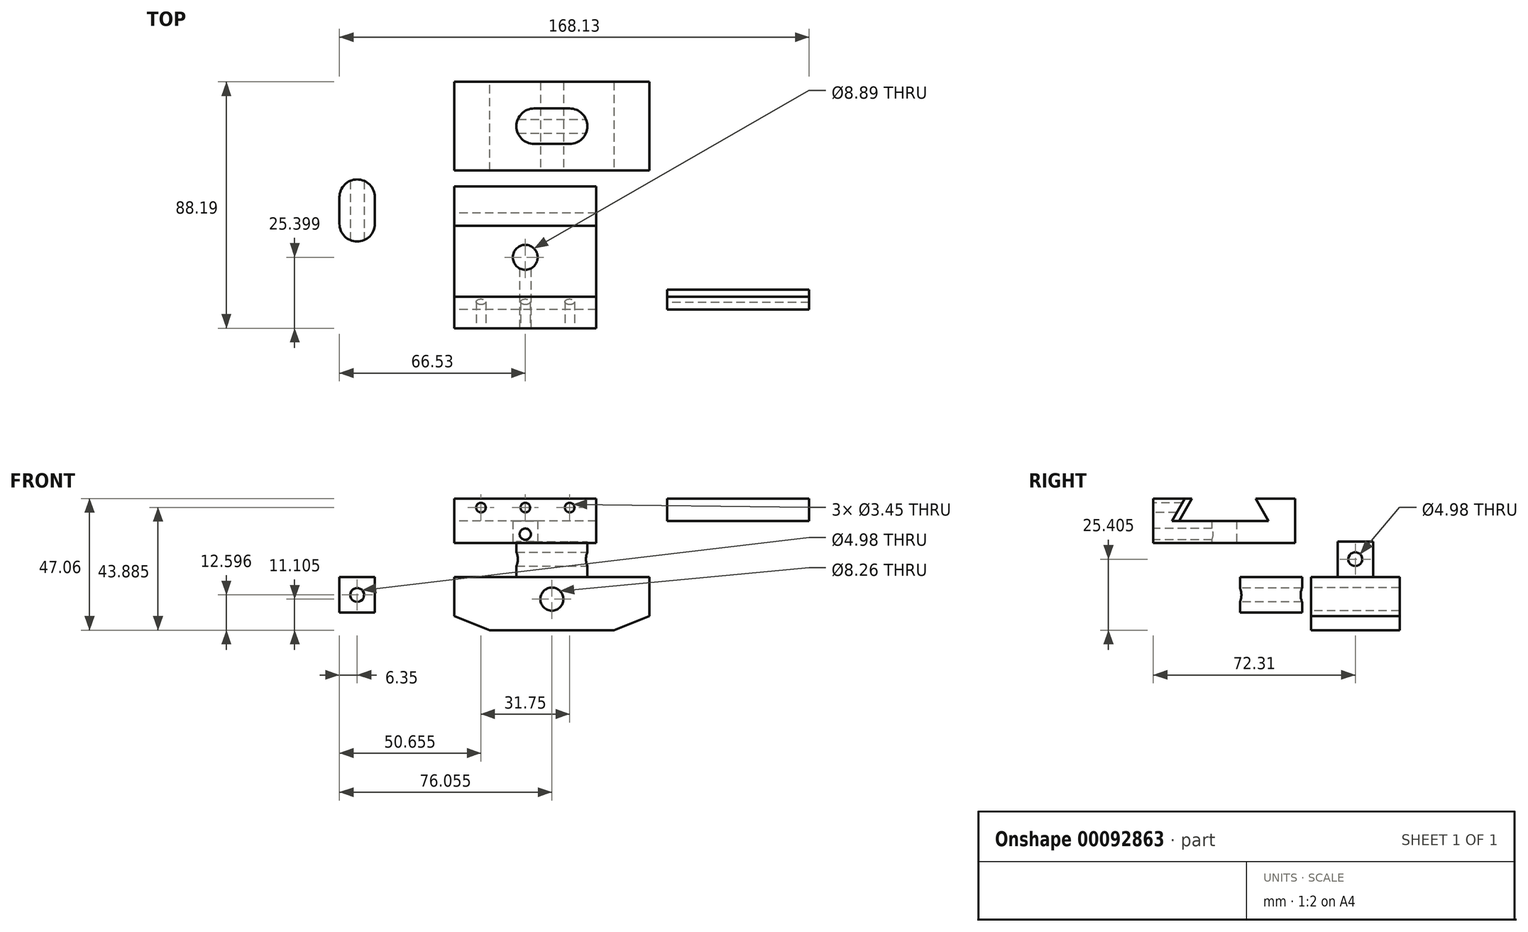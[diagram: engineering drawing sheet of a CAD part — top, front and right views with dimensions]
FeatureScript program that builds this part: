
annotation { "Feature Type Name" : "Feature", "Feature Type Description" : "" }
export const myFeature = defineFeature(function(context is Context, id is Id, definition is map)
    precondition{}
    {
        {
            var Q0;
            Q0=qCreatedBy(makeId("Right.planeOp"),FACE);
            var sketch = newSketch(context, id + "F0", { "sketchPlane" : qUnion([Q0])});
            skLineSegment(sketch, "E0.bottom", {"start": v(15.88, -15.87) * mm, "end": v(-15.88, -15.88) * mm});
            skLineSegment(sketch, "E0.top", {"start": v(15.88, 15.88) * mm, "end": v(-15.88, 15.88) * mm});
            skLineSegment(sketch, "E0.left", {"start": v(15.88, -15.87) * mm, "end": v(15.88, 7.62) * mm});
            skLineSegment(sketch, "E0.right", {"start": v(-15.88, -15.88) * mm, "end": v(-15.88, 7.62) * mm});
            skPoint(sketch, "E0.middle", {"position": v(0, 0) * mm});
            skLineSegment(sketch, "E1", {"start": v(-15.88, 7.62) * mm, "end": v(15.88, 7.62) * mm, "construction": true});
            skLineSegment(sketch, "E2", {"start": v(15.88, 15.88) * mm, "end": v(11.1, 7.62) * mm});
            skLineSegment(sketch, "E3", {"start": v(-15.88, 15.88) * mm, "end": v(-11.1, 7.62) * mm});
            skLineSegment(sketch, "E4", {"start": v(-15.88, 7.62) * mm, "end": v(-11.1, 7.62) * mm});
            skLineSegment(sketch, "E5", {"start": v(11.1, 7.62) * mm, "end": v(15.88, 7.62) * mm});
            skSolve(sketch);
        }
        {
            var Q0;
            Q0=makeQuery(id+"F0.imprint","IMPRINT",FACE,{"disambiguationData":[TD([[makeQuery(id+"F0.imprint","IMPRINT",EDGE,{"derivedFrom":sQuery(id+"F0.wireOp",EDGE,"E0.bottom")}),-1.0]])]});
            extrude(context, id + "F1", {"entities" : qUnion([Q0]), "depth" : 69.85 * mm});
        }
        {
            var Q0;
            Q0=makeQuery(id+"F1.opExtrude","CAP_FACE",FACE,{"disambiguationData":[OSD([sQuery(id+"F0.wireOp",EDGE,"E0.bottom"),sQuery(id+"F0.wireOp",EDGE,"E0.top"),sQuery(id+"F0.wireOp",EDGE,"E0.left"),sQuery(id+"F0.wireOp",EDGE,"E0.right"),sQuery(id+"F0.wireOp",EDGE,"E2"),sQuery(id+"F0.wireOp",EDGE,"E3"),sQuery(id+"F0.wireOp",EDGE,"E4"),sQuery(id+"F0.wireOp",EDGE,"E5")])],"isStart":false});
            var sketch = newSketch(context, id + "F2", { "sketchPlane" : qUnion([Q0])});
            skLineSegment(sketch, "E6", {"start": v(-12.2, 9.52) * mm, "end": v(12.2, 9.52) * mm, "construction": true});
            skPoint(sketch, "E7", {"position": v(0, 9.52) * mm});
            skSolve(sketch);
        }
        {
            var Q0;
            Q0=sQuery(id+"F2.wireOp",VERTEX,"E7");
            var Q1;
            Q1=makeQuery(id+"F1.opExtrude","SWEPT_BODY",BODY,{"disambiguationData":[OSD([sQuery(id+"F0.wireOp",EDGE,"E0.bottom"),sQuery(id+"F0.wireOp",EDGE,"E0.top"),sQuery(id+"F0.wireOp",EDGE,"E0.left"),sQuery(id+"F0.wireOp",EDGE,"E0.right"),sQuery(id+"F0.wireOp",EDGE,"E2"),sQuery(id+"F0.wireOp",EDGE,"E3"),sQuery(id+"F0.wireOp",EDGE,"E4"),sQuery(id+"F0.wireOp",EDGE,"E5")])]});
            hole(context, id + "F3", {"style" : HoleStyle.SIMPLE, "endStyle" : HoleEndStyle.THROUGH, "standardTappedOrClearance" : lookupTablePath({ "standard" : "ANSI", "fit" : "Close", "size" : "#10", "type" : "Clearance" }), "standardBlindInLast" : lookupTablePath({ "fit" : "Close", "standard" : "ANSI", "size" : "#10", "type" : "Clearance" }), "holeDiameter" : 4.98 * mm, "locations" : qUnion([Q0]), "scope" : qUnion([Q1]), "isTappedThrough" : true});
        }
        {
            var Q0;
            Q0=makeQuery(id+"F1.opExtrude","SWEPT_FACE",FACE,{"disambiguationData":[OSD([sQuery(id+"F0.wireOp",EDGE,"E0.right")])]});
            var sketch = newSketch(context, id + "F4", { "sketchPlane" : qUnion([Q0])});
            skLineSegment(sketch, "E8.0.0", {"start": v(0, 7.62) * mm, "end": v(0, -15.88) * mm, "construction": true});
            skLineSegment(sketch, "E8.0.1", {"start": v(0, -15.88) * mm, "end": v(69.85, -15.88) * mm, "construction": true});
            skLineSegment(sketch, "E8.0.2", {"start": v(69.85, -15.88) * mm, "end": v(69.85, 7.62) * mm, "construction": true});
            skLineSegment(sketch, "E8.0.3", {"start": v(69.85, 7.62) * mm, "end": v(0, 7.62) * mm, "construction": true});
            skLineSegment(sketch, "E9", {"start": v(0, -4.78) * mm, "end": v(69.85, -4.78) * mm, "construction": true});
            skPoint(sketch, "E10", {"position": v(34.93, -4.78) * mm});
            skSolve(sketch);
        }
        {
            var Q0;
            Q0=sQuery(id+"F4.wireOp",VERTEX,"E10");
            var Q1;
            Q1=makeQuery(id+"F1.opExtrude","SWEPT_BODY",BODY,{"disambiguationData":[OSD([sQuery(id+"F0.wireOp",EDGE,"E0.bottom"),sQuery(id+"F0.wireOp",EDGE,"E0.top"),sQuery(id+"F0.wireOp",EDGE,"E0.left"),sQuery(id+"F0.wireOp",EDGE,"E0.right"),sQuery(id+"F0.wireOp",EDGE,"E2"),sQuery(id+"F0.wireOp",EDGE,"E3"),sQuery(id+"F0.wireOp",EDGE,"E4"),sQuery(id+"F0.wireOp",EDGE,"E5")])]});
            hole(context, id + "F5", {"style" : HoleStyle.SIMPLE, "endStyle" : HoleEndStyle.THROUGH, "holeDiameter" : 8.25 * mm, "locations" : qUnion([Q0]), "scope" : qUnion([Q1]), "isTappedThrough" : true});
        }
        {
            var Q0;
            Q0=makeQuery(id+"F1.opExtrude","SWEPT_FACE",FACE,{"disambiguationData":[OSD([sQuery(id+"F0.wireOp",EDGE,"E0.top")])]});
            var sketch = newSketch(context, id + "F6", { "sketchPlane" : qUnion([Q0])});
            skLineSegment(sketch, "E11.0.0", {"start": v(0, 15.88) * mm, "end": v(0, -15.88) * mm, "construction": true});
            skLineSegment(sketch, "E11.0.1", {"start": v(0, -15.88) * mm, "end": v(69.85, -15.88) * mm, "construction": true});
            skLineSegment(sketch, "E11.0.2", {"start": v(69.85, -15.88) * mm, "end": v(69.85, 15.88) * mm, "construction": true});
            skLineSegment(sketch, "E11.0.3", {"start": v(69.85, 15.88) * mm, "end": v(0, 15.88) * mm, "construction": true});
            skLineSegment(sketch, "E12", {"start": v(28.58, 15.88) * mm, "end": v(28.58, -15.88) * mm, "construction": true});
            skLineSegment(sketch, "E13", {"start": v(41.28, 15.88) * mm, "end": v(41.28, -15.88) * mm, "construction": true});
            skLineSegment(sketch, "E14", {"start": v(0, 0) * mm, "end": v(69.85, 0) * mm, "construction": true});
            skLineSegment(sketch, "E15", {"start": v(28.58, 0) * mm, "end": v(41.28, 0) * mm});
            skArc(sketch, "E16.0.startCap", {"start": v(28.58, -6.35) * mm, "mid": v(22.23, 0) * mm, "end": v(28.58, 6.35) * mm});
            skArc(sketch, "E16.0.endCap", {"start": v(41.28, 6.35) * mm, "mid": v(47.63, 0) * mm, "end": v(41.28, -6.35) * mm});
            skLineSegment(sketch, "E16.0.left", {"start": v(28.58, 6.35) * mm, "end": v(41.28, 6.35) * mm});
            skLineSegment(sketch, "E16.0.right", {"start": v(28.58, -6.35) * mm, "end": v(41.28, -6.35) * mm});
            skSolve(sketch);
        }
        {
            var Q0;
            Q0=makeQuery(id+"F6.imprint","IMPRINT",FACE,{"disambiguationData":[TD([[makeQuery(id+"F6.imprint","IMPRINT",EDGE,{"derivedFrom":sQuery(id+"F6.wireOp",EDGE,"E16.0.startCap")}),-1.0]])]});
            extrude(context, id + "F7", {"entities" : qUnion([Q0]), "operationType" : NewBodyOperationType.REMOVE, "oppositeDirection" : true, "depth" : 12.7 * mm});
        }
        {
            var Q0;
            Q0=qCreatedBy(makeId("Front.planeOp"),FACE);
            var sketch = newSketch(context, id + "F8", { "sketchPlane" : qUnion([Q0])});
            skLineSegment(sketch, "E17.bottom", {"start": v(-50.66, 3.07) * mm, "end": v(-18.9, 3.07) * mm});
            skLineSegment(sketch, "E17.top", {"start": v(-50.66, -9.63) * mm, "end": v(-18.9, -9.63) * mm});
            skLineSegment(sketch, "E17.left", {"start": v(-50.66, 3.07) * mm, "end": v(-50.66, -9.63) * mm});
            skLineSegment(sketch, "E17.right", {"start": v(-18.9, 3.07) * mm, "end": v(-18.9, -9.63) * mm});
            skLineSegment(sketch, "E18", {"start": v(-18.9, -1.38) * mm, "end": v(-50.66, -1.38) * mm, "construction": true});
            skLineSegment(sketch, "E19", {"start": v(-50.66, -9.63) * mm, "end": v(-45.89, -1.38) * mm});
            skLineSegment(sketch, "E20", {"start": v(-18.9, -9.63) * mm, "end": v(-23.67, -1.38) * mm});
            skLineSegment(sketch, "E21", {"start": v(-50.66, -1.38) * mm, "end": v(-45.89, -1.38) * mm});
            skLineSegment(sketch, "E22", {"start": v(-23.67, -1.38) * mm, "end": v(-18.9, -1.38) * mm});
            skSolve(sketch);
        }
        {
            var Q0;
            {var subQ1=sQuery(id+"F8.wireOp",EDGE,"E17.bottom");Q0=makeQuery(id+"F8.imprint","IMPRINT",FACE,{"disambiguationData":[TD([[makeQuery(id+"F8.imprint","IMPRINT",EDGE,{"derivedFrom":subQ1}),-1.0]])]});}
            extrude(context, id + "F9", {"entities" : qUnion([Q0]), "depth" : 60.32 * mm});
        }
        {
            var Q0;
            Q0=makeQuery(id+"F9.opExtrude","CAP_FACE",FACE,{"disambiguationData":[OSD([sQuery(id+"F8.wireOp",EDGE,"E17.bottom"),sQuery(id+"F8.wireOp",EDGE,"E17.top"),sQuery(id+"F8.wireOp",EDGE,"E17.left"),sQuery(id+"F8.wireOp",EDGE,"E17.right"),sQuery(id+"F8.wireOp",EDGE,"E19"),sQuery(id+"F8.wireOp",EDGE,"E20"),sQuery(id+"F8.wireOp",EDGE,"E21"),sQuery(id+"F8.wireOp",EDGE,"E22")])],"isStart":false});
            var sketch = newSketch(context, id + "F10", { "sketchPlane" : qUnion([Q0])});
            skLineSegment(sketch, "E23", {"start": v(-46.99, -3.28) * mm, "end": v(-22.57, -3.28) * mm, "construction": true});
            skPoint(sketch, "E24", {"position": v(-34.78, -3.28) * mm});
            skSolve(sketch);
        }
        {
            var Q0;
            Q0=sQuery(id+"F10.wireOp",VERTEX,"E24");
            var Q1;
            Q1=makeQuery(id+"F9.opExtrude","SWEPT_BODY",BODY,{"disambiguationData":[OSD([sQuery(id+"F8.wireOp",EDGE,"E17.bottom"),sQuery(id+"F8.wireOp",EDGE,"E17.top"),sQuery(id+"F8.wireOp",EDGE,"E17.left"),sQuery(id+"F8.wireOp",EDGE,"E17.right"),sQuery(id+"F8.wireOp",EDGE,"E19"),sQuery(id+"F8.wireOp",EDGE,"E20"),sQuery(id+"F8.wireOp",EDGE,"E21"),sQuery(id+"F8.wireOp",EDGE,"E22")])]});
            hole(context, id + "F11", {"style" : HoleStyle.SIMPLE, "endStyle" : HoleEndStyle.THROUGH, "standardTappedOrClearance" : lookupTablePath({ "standard" : "ANSI", "fit" : "Close", "size" : "#10", "type" : "Clearance" }), "standardBlindInLast" : lookupTablePath({ "fit" : "Close", "standard" : "ANSI", "size" : "#10", "type" : "Clearance" }), "holeDiameter" : 4.98 * mm, "locations" : qUnion([Q0]), "scope" : qUnion([Q1]), "isTappedThrough" : true});
        }
        {
            var Q0;
            Q0=makeQuery(id+"F9.opExtrude","SWEPT_FACE",FACE,{"disambiguationData":[OSD([sQuery(id+"F8.wireOp",EDGE,"E17.top")])]});
            var sketch = newSketch(context, id + "F12", { "sketchPlane" : qUnion([Q0])});
            skLineSegment(sketch, "E25", {"start": v(-50.66, 34.92) * mm, "end": v(-18.9, 34.92) * mm, "construction": true});
            skLineSegment(sketch, "E26", {"start": v(-50.66, 25.4) * mm, "end": v(-18.9, 25.4) * mm, "construction": true});
            skLineSegment(sketch, "E27", {"start": v(-34.78, 34.92) * mm, "end": v(-34.78, 25.4) * mm});
            skArc(sketch, "E28.0.startCap", {"start": v(-41.13, 34.92) * mm, "mid": v(-34.78, 41.27) * mm, "end": v(-28.43, 34.92) * mm});
            skArc(sketch, "E28.0.endCap", {"start": v(-28.43, 25.4) * mm, "mid": v(-34.78, 19.05) * mm, "end": v(-41.13, 25.4) * mm});
            skLineSegment(sketch, "E28.0.left", {"start": v(-28.43, 34.92) * mm, "end": v(-28.43, 25.4) * mm});
            skLineSegment(sketch, "E28.0.right", {"start": v(-41.13, 34.92) * mm, "end": v(-41.13, 25.4) * mm});
            skSolve(sketch);
        }
        {
            var Q0;
            Q0=makeQuery(id+"F12.imprint","IMPRINT",FACE,{"disambiguationData":[TD([[makeQuery(id+"F12.imprint","IMPRINT",EDGE,{"derivedFrom":sQuery(id+"F12.wireOp",EDGE,"E28.0.startCap")}),-1.0]])]});
            extrude(context, id + "F13", {"entities" : qUnion([Q0]), "operationType" : NewBodyOperationType.REMOVE, "endBound" : BoundingType.THROUGH_ALL, "oppositeDirection" : true, "depth" : 25.4 * mm});
        }
        {
            var Q0;
            Q0=makeQuery(id+"F9.opExtrude","SWEPT_FACE",FACE,{"disambiguationData":[OSD([sQuery(id+"F8.wireOp",EDGE,"E17.top")])]});
            var sketch = newSketch(context, id + "F14", { "sketchPlane" : qUnion([Q0])});
            skLineSegment(sketch, "E29", {"start": v(-44.05, 60.33) * mm, "end": v(-44.05, 0) * mm, "construction": true});
            skLineSegment(sketch, "E30", {"start": v(-25.5, 60.33) * mm, "end": v(-25.5, 0) * mm, "construction": true});
            skPoint(sketch, "E31", {"position": v(-25.5, 30.16) * mm});
            skPoint(sketch, "E32", {"position": v(-44.05, 30.16) * mm});
            skSolve(sketch);
        }
        {
            var Q0;
            Q0=sQuery(id+"F14.wireOp",VERTEX,"E31");
            var Q1;
            Q1=sQuery(id+"F14.wireOp",VERTEX,"E32");
            var Q2;
            Q2=makeQuery(id+"F9.opExtrude","SWEPT_BODY",BODY,{"disambiguationData":[OSD([sQuery(id+"F8.wireOp",EDGE,"E17.bottom"),sQuery(id+"F8.wireOp",EDGE,"E17.top"),sQuery(id+"F8.wireOp",EDGE,"E17.left"),sQuery(id+"F8.wireOp",EDGE,"E17.right"),sQuery(id+"F8.wireOp",EDGE,"E19"),sQuery(id+"F8.wireOp",EDGE,"E20"),sQuery(id+"F8.wireOp",EDGE,"E21"),sQuery(id+"F8.wireOp",EDGE,"E22")])]});
            hole(context, id + "F15", {"style" : HoleStyle.SIMPLE, "endStyle" : HoleEndStyle.THROUGH, "standardTappedOrClearance" : lookupTablePath({ "standard" : "ANSI", "engagement" : "75%", "pitch" : "32 tpi", "size" : "#10", "type" : "Tapped" }), "standardBlindInLast" : lookupTablePath({ "standard" : "ANSI", "engagement" : "75%", "pitch" : "32 tpi", "size" : "#10", "type" : "Tapped" }), "holeDiameter" : 4.04 * mm, "locations" : qUnion([Q0, Q1]), "scope" : qUnion([Q2]), "isTappedThrough" : true, "majorDiameter" : 4.83 * mm, "showTappedDepth" : true});
        }
        {
            var Q0;
            Q0=qCreatedBy(makeId("Right.planeOp"),FACE);
            var sketch = newSketch(context, id + "F16", { "sketchPlane" : qUnion([Q0])});
            skLineSegment(sketch, "E33.bottom", {"start": v(-72.31, 31.18) * mm, "end": v(-21.51, 31.18) * mm});
            skLineSegment(sketch, "E33.top", {"start": v(-72.31, 15.3) * mm, "end": v(-21.51, 15.3) * mm});
            skLineSegment(sketch, "E33.left", {"start": v(-72.31, 31.18) * mm, "end": v(-72.31, 15.3) * mm});
            skLineSegment(sketch, "E33.right", {"start": v(-21.51, 31.18) * mm, "end": v(-21.51, 15.3) * mm});
            skLineSegment(sketch, "E34", {"start": v(-72.31, 23.25) * mm, "end": v(-21.51, 23.25) * mm, "construction": true});
            skLineSegment(sketch, "E35", {"start": v(-35.6, 31.18) * mm, "end": v(-35.6, 15.3) * mm, "construction": true});
            skLineSegment(sketch, "E36", {"start": v(-61, 31.18) * mm, "end": v(-61, 15.3) * mm, "construction": true});
            skLineSegment(sketch, "E37", {"start": v(-35.6, 31.18) * mm, "end": v(-31.03, 23.25) * mm});
            skLineSegment(sketch, "E38", {"start": v(-61, 31.18) * mm, "end": v(-65.58, 23.25) * mm});
            skLineSegment(sketch, "E39", {"start": v(-65.58, 23.25) * mm, "end": v(-31.03, 23.25) * mm});
            skSolve(sketch);
        }
        {
            var Q0;
            Q0=makeQuery(id+"F16.imprint","IMPRINT",FACE,{"disambiguationData":[TD([[makeQuery(id+"F16.imprint","IMPRINT",EDGE,{"derivedFrom":sQuery(id+"F16.wireOp",EDGE,"E33.top")}),1.0]])]});
            extrude(context, id + "F17", {"entities" : qUnion([Q0]), "depth" : 50.8 * mm});
        }
        {
            var Q0;
            Q0=makeQuery(id+"F17.opExtrude","SWEPT_FACE",FACE,{"disambiguationData":[OSD([sQuery(id+"F16.wireOp",EDGE,"E33.top")])]});
            var sketch = newSketch(context, id + "F18", { "sketchPlane" : qUnion([Q0])});
            skLineSegment(sketch, "E40.0.0", {"start": v(0, 72.31) * mm, "end": v(0, 21.51) * mm, "construction": true});
            skLineSegment(sketch, "E40.0.1", {"start": v(0, 21.51) * mm, "end": v(50.8, 21.51) * mm, "construction": true});
            skLineSegment(sketch, "E40.0.2", {"start": v(50.8, 21.51) * mm, "end": v(50.8, 72.31) * mm, "construction": true});
            skLineSegment(sketch, "E40.0.3", {"start": v(50.8, 72.31) * mm, "end": v(0, 72.31) * mm, "construction": true});
            skLineSegment(sketch, "E41", {"start": v(50.8, 46.91) * mm, "end": v(0, 46.91) * mm, "construction": true});
            skPoint(sketch, "E42", {"position": v(25.4, 46.91) * mm});
            skSolve(sketch);
        }
        {
            var Q0;
            Q0=sQuery(id+"F18.wireOp",VERTEX,"E42");
            var Q1;
            Q1=makeQuery(id+"F17.opExtrude","SWEPT_BODY",BODY,{"disambiguationData":[OSD([sQuery(id+"F16.wireOp",EDGE,"E33.bottom"),sQuery(id+"F16.wireOp",EDGE,"E33.top"),sQuery(id+"F16.wireOp",EDGE,"E33.left"),sQuery(id+"F16.wireOp",EDGE,"E33.right"),sQuery(id+"F16.wireOp",EDGE,"E37"),sQuery(id+"F16.wireOp",EDGE,"E38"),sQuery(id+"F16.wireOp",EDGE,"E39")])]});
            hole(context, id + "F19", {"style" : HoleStyle.SIMPLE, "endStyle" : HoleEndStyle.THROUGH, "holeDiameter" : 8.9 * mm, "locations" : qUnion([Q0]), "scope" : qUnion([Q1]), "isTappedThrough" : true});
        }
        {
            var Q0;
            Q0=makeQuery(id+"F17.opExtrude","SWEPT_FACE",FACE,{"disambiguationData":[OSD([sQuery(id+"F16.wireOp",EDGE,"E33.left")])]});
            var sketch = newSketch(context, id + "F20", { "sketchPlane" : qUnion([Q0])});
            skLineSegment(sketch, "E43", {"start": v(0, 18.48) * mm, "end": v(50.8, 18.48) * mm, "construction": true});
            skLineSegment(sketch, "E44", {"start": v(0, 28) * mm, "end": v(50.8, 28) * mm, "construction": true});
            skPoint(sketch, "E45", {"position": v(25.4, 18.48) * mm});
            skPoint(sketch, "E46", {"position": v(25.4, 28) * mm});
            skLineSegment(sketch, "E47", {"start": v(9.53, 31.18) * mm, "end": v(9.53, 15.3) * mm, "construction": true});
            skLineSegment(sketch, "E48", {"start": v(41.28, 31.18) * mm, "end": v(41.28, 15.3) * mm, "construction": true});
            skPoint(sketch, "E49", {"position": v(9.53, 28) * mm});
            skPoint(sketch, "E50", {"position": v(41.28, 28) * mm});
            skSolve(sketch);
        }
        {
            var Q0;
            Q0=sQuery(id+"F20.wireOp",VERTEX,"E45");
            var Q1;
            Q1=makeQuery(id+"F17.opExtrude","SWEPT_BODY",BODY,{"disambiguationData":[OSD([sQuery(id+"F16.wireOp",EDGE,"E33.bottom"),sQuery(id+"F16.wireOp",EDGE,"E33.top"),sQuery(id+"F16.wireOp",EDGE,"E33.left"),sQuery(id+"F16.wireOp",EDGE,"E33.right"),sQuery(id+"F16.wireOp",EDGE,"E37"),sQuery(id+"F16.wireOp",EDGE,"E38"),sQuery(id+"F16.wireOp",EDGE,"E39")])]});
            hole(context, id + "F21", {"style" : HoleStyle.SIMPLE, "endStyle" : HoleEndStyle.BLIND, "standardTappedOrClearance" : lookupTablePath({ "standard" : "ANSI", "engagement" : "75%", "pitch" : "32 tpi", "size" : "#10", "type" : "Tapped" }), "standardBlindInLast" : lookupTablePath({ "standard" : "ANSI", "engagement" : "75%", "pitch" : "32 tpi", "size" : "#10", "type" : "Tapped" }), "holeDiameter" : 4.04 * mm, "holeDepth" : 25.4 * mm, "locations" : qUnion([Q0]), "scope" : qUnion([Q1]), "majorDiameter" : 4.83 * mm});
        }
        {
            var Q0;
            Q0=sQuery(id+"F20.wireOp",VERTEX,"E49");
            var Q1;
            Q1=sQuery(id+"F20.wireOp",VERTEX,"E46");
            var Q2;
            Q2=sQuery(id+"F20.wireOp",VERTEX,"E50");
            var Q3;
            Q3=makeQuery(id+"F17.opExtrude","SWEPT_BODY",BODY,{"disambiguationData":[OSD([sQuery(id+"F16.wireOp",EDGE,"E33.bottom"),sQuery(id+"F16.wireOp",EDGE,"E33.top"),sQuery(id+"F16.wireOp",EDGE,"E33.left"),sQuery(id+"F16.wireOp",EDGE,"E33.right"),sQuery(id+"F16.wireOp",EDGE,"E37"),sQuery(id+"F16.wireOp",EDGE,"E38"),sQuery(id+"F16.wireOp",EDGE,"E39")])]});
            hole(context, id + "F22", {"style" : HoleStyle.SIMPLE, "endStyle" : HoleEndStyle.BLIND, "standardTappedOrClearance" : lookupTablePath({ "standard" : "ANSI", "engagement" : "75%", "pitch" : "32 tpi", "size" : "#8", "type" : "Tapped" }), "standardBlindInLast" : lookupTablePath({ "standard" : "ANSI", "engagement" : "75%", "pitch" : "32 tpi", "size" : "#8", "type" : "Tapped" }), "holeDiameter" : 3.45 * mm, "holeDepth" : 19.05 * mm, "locations" : qUnion([Q0, Q1, Q2]), "scope" : qUnion([Q3]), "majorDiameter" : 4.17 * mm});
        }
        {
            var Q0;
            Q0=makeQuery(id+"F17.opExtrude","CAP_FACE",FACE,{"disambiguationData":[OSD([sQuery(id+"F16.wireOp",EDGE,"E33.bottom"),sQuery(id+"F16.wireOp",EDGE,"E33.top"),sQuery(id+"F16.wireOp",EDGE,"E33.left"),sQuery(id+"F16.wireOp",EDGE,"E33.right"),sQuery(id+"F16.wireOp",EDGE,"E37"),sQuery(id+"F16.wireOp",EDGE,"E38"),sQuery(id+"F16.wireOp",EDGE,"E39")])],"isStart":false});
            cPlane(context, id + "F23", {"entities" : qUnion([Q0]), "cplaneType" : CPlaneType.OFFSET, "offset" : 25.4 * mm, "width" : 152.4 * mm, "height" : 152.4 * mm});
        }
        {
            var Q0;
            Q0=qCreatedBy(id+"F23.planeOp",FACE);
            var sketch = newSketch(context, id + "F24", { "sketchPlane" : qUnion([Q0])});
            skLineSegment(sketch, "E51.0.0", {"start": v(-61, 31.18) * mm, "end": v(-72.31, 31.18) * mm, "construction": true});
            skLineSegment(sketch, "E51.0.1", {"start": v(-72.31, 31.18) * mm, "end": v(-72.31, 15.3) * mm, "construction": true});
            skLineSegment(sketch, "E51.0.2", {"start": v(-72.31, 15.3) * mm, "end": v(-21.51, 15.3) * mm, "construction": true});
            skLineSegment(sketch, "E51.0.3", {"start": v(-21.51, 15.3) * mm, "end": v(-21.51, 31.18) * mm, "construction": true});
            skLineSegment(sketch, "E51.0.4", {"start": v(-21.51, 31.18) * mm, "end": v(-35.6, 31.18) * mm, "construction": true});
            skLineSegment(sketch, "E51.0.5", {"start": v(-35.6, 31.18) * mm, "end": v(-31.03, 23.25) * mm, "construction": true});
            skLineSegment(sketch, "E51.0.6", {"start": v(-31.03, 23.25) * mm, "end": v(-65.58, 23.25) * mm, "construction": true});
            skLineSegment(sketch, "E51.0.7", {"start": v(-65.58, 23.25) * mm, "end": v(-61, 31.18) * mm, "construction": true});
            skLineSegment(sketch, "E52", {"start": v(-61, 31.18) * mm, "end": v(-65.58, 23.25) * mm});
            skLineSegment(sketch, "E53", {"start": v(-65.58, 23.25) * mm, "end": v(-63.04, 23.25) * mm});
            skLineSegment(sketch, "E54", {"start": v(-63.04, 23.25) * mm, "end": v(-58.47, 31.18) * mm});
            skLineSegment(sketch, "E55", {"start": v(-58.47, 31.18) * mm, "end": v(-61, 31.18) * mm});
            skSolve(sketch);
        }
        {
            var Q0;
            Q0=makeQuery(id+"F24.imprint","IMPRINT",FACE,{"disambiguationData":[TD([[makeQuery(id+"F24.imprint","IMPRINT",EDGE,{"derivedFrom":sQuery(id+"F24.wireOp",EDGE,"E52")}),1.0]])]});
            extrude(context, id + "F25", {"entities" : qUnion([Q0]), "depth" : 50.8 * mm});
        }
        {
            var Q0;
            Q0=makeQuery(id+"F1.opExtrude","CAP_EDGE",EDGE,{"disambiguationData":[OSD([sQuery(id+"F0.wireOp",EDGE,"E0.bottom")])],"isStart":false});
            var Q1;
            Q1=makeQuery(id+"F1.opExtrude","CAP_EDGE",EDGE,{"disambiguationData":[OSD([sQuery(id+"F0.wireOp",EDGE,"E0.bottom")])],"isStart":true});
            chamfer(context, id + "F26", {"entities" : qUnion([Q0, Q1]), "chamferType" : ChamferType.TWO_OFFSETS, "width1" : 12.7 * mm, "oppositeDirection" : false, "width2" : 5.08 * mm, "tangentPropagation" : true});
        }
    });
